# Revit family: Paper-Dispenser-Waste-Receptor_Bobrick_Contura_B-43699
name_source: partatom
category: Plumbing Fixtures
units: mm (PartAtom-declared; Revit-internal decimal feet)

## family parameters
Cut with Voids When Loaded = No
Host = Face
OmniClass Number = 23.40.20.21
OmniClass Title = Toilet and Bath Specialties
Part Type = Normal
Room Calculation Point = No
Round Connector Dimension = Use Diameter
Shared = Yes

## types (1)
- B-43699
    ADA Compliant = Yes
    Assembly Code = C1030210
    CW Connection = No
    CWFU = 0
    Capacity = 3.0-gal. (11.3-L)
    Default Elevation = 52 3/4"
    Depth = 6 5/8"
    Description = Combination Paper Towel Dispenser/Waste Receptacle
    Finish = Stainless Steel-Bobrick-Satin
    HW Connection = No
    HWFU = 0
    Height = 28 1/8"
    Installation Type = Wall Surface Mounted
    Manufacturer = Bobrick
    Material = Stainless Steel-Bobrick-Satin
    Model = B-43699
    Paper Type = Multi-Fold Towel
    Product Documentation Link = https://www.bobrick.com
    Product Page URL = https://www.bobrick.com
    Projection from Wall = 2 1/2"
    Revised Date = 07/24/2024
    Type Comments = Dispenses 350 C-fold or 475 multifold towels.
    URL = http://www.bobrick.com
    Vent Connection = No
    WFU = 0
    Waste Connection = No
    Width = 12 7/8"

## geometry (parser evidence)
native form markers: Sweep x3
no freeform markers — native parametric forms only
